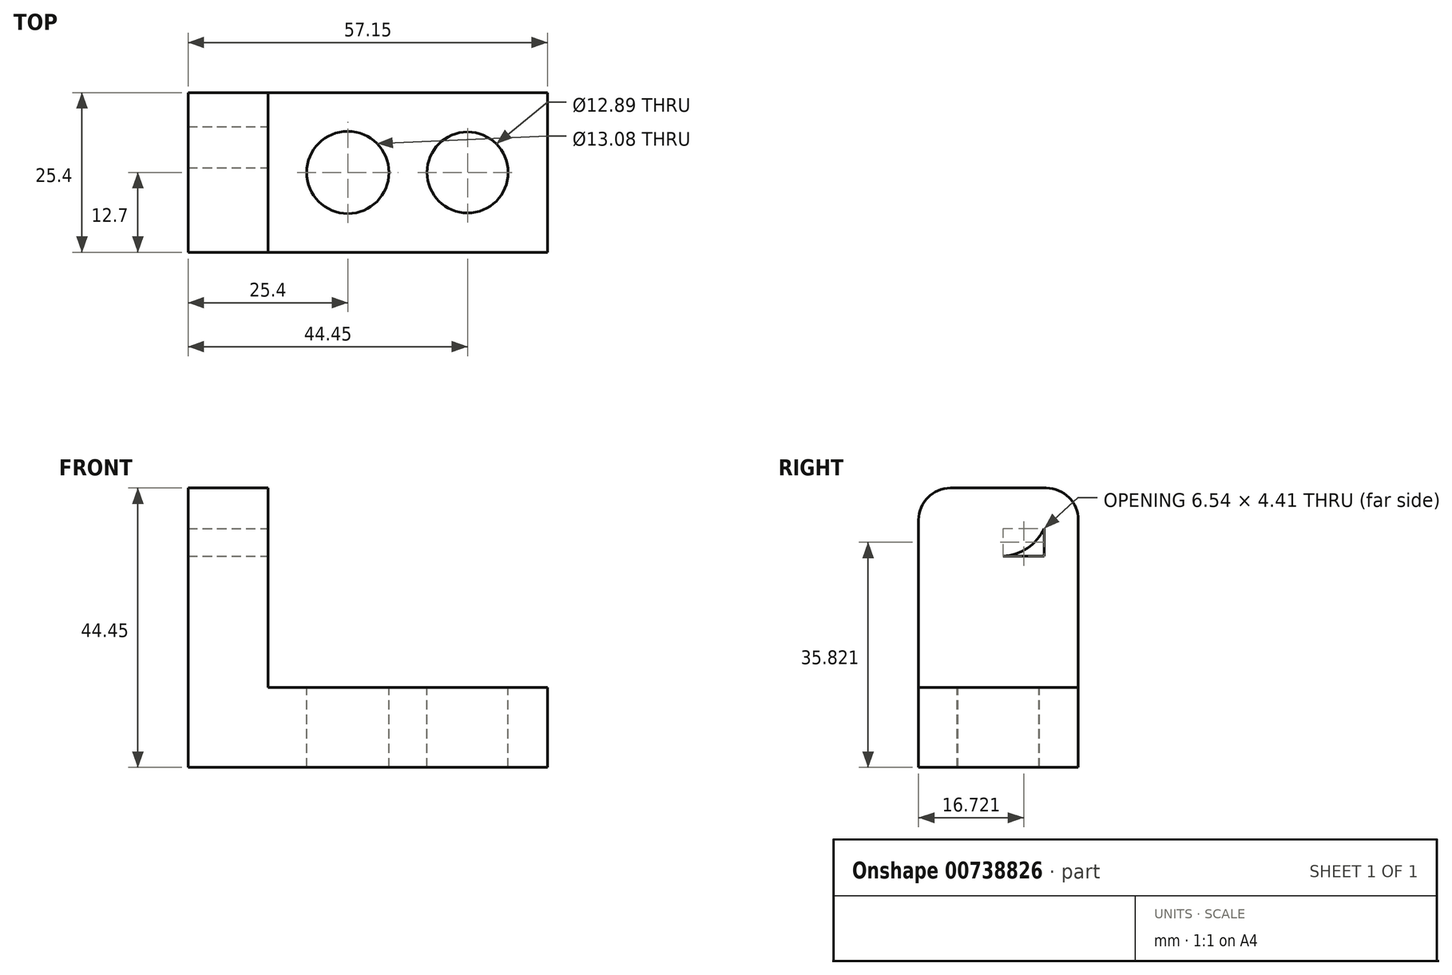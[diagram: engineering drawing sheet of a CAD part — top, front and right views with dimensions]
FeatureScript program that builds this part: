
annotation { "Feature Type Name" : "Feature", "Feature Type Description" : "" }
export const myFeature = defineFeature(function(context is Context, id is Id, definition is map)
    precondition{}
    {
        {
            var Q0;
            Q0=qCreatedBy(makeId("Front.planeOp"),FACE);
            var sketch = newSketch(context, id + "F0", { "sketchPlane" : qUnion([Q0])});
            skLineSegment(sketch, "E0", {"start": v(0, 0) * mm, "end": v(0, 44.45) * mm});
            skLineSegment(sketch, "E1", {"start": v(0, 44.45) * mm, "end": v(57.15, 44.45) * mm});
            skLineSegment(sketch, "E2", {"start": v(57.15, 44.45) * mm, "end": v(57.15, 0) * mm});
            skLineSegment(sketch, "E3", {"start": v(57.15, 0) * mm, "end": v(0, 0) * mm});
            skSolve(sketch);
        }
        {
            var Q0;
            Q0 = qSketchRegion(id + "F0", true);
            extrude(context, id + "F1", {"entities" : qUnion([Q0]), "depth" : 25.4 * mm, "offsetDistance" : 25.4 * mm});
        }
        {
            var Q0;
            Q0=makeQuery(id+"F1.opExtrude","SWEPT_FACE",FACE,{"disambiguationData":[OSD([sQuery(id+"F0.wireOp",EDGE,"E1")])]});
            var sketch = newSketch(context, id + "F2", { "sketchPlane" : qUnion([Q0])});
            skLineSegment(sketch, "E4", {"start": v(12.7, 0) * mm, "end": v(12.7, -25.4) * mm});
            skSolve(sketch);
        }
        {
            var Q0;
            {var subQ0=sQuery(id+"F2.wireOp",EDGE,"E4");Q0=makeQuery(id+"F2.imprint","IMPRINT",FACE,{"disambiguationData":[TD([[makeQuery(id+"F2.imprint","IMPRINT",EDGE,{"derivedFrom":subQ0}),1.0]])]});}
            extrude(context, id + "F3", {"entities" : qUnion([Q0]), "operationType" : NewBodyOperationType.REMOVE, "oppositeDirection" : true, "depth" : 31.75 * mm, "offsetDistance" : 25.4 * mm});
        }
        {
            var Q0;
            Q0=makeQuery(id+"F3.boolean.opBoolean","COPY",FACE,{"derivedFrom":makeQuery(id+"F3.opExtrude","CAP_FACE",FACE,{"disambiguationData":[OSD([sQuery(id+"F0.wireOp",EDGE,"E1"),sQuery(id+"F0.wireOp",EDGE,"E2"),sQuery(id+"F2.wireOp",EDGE,"E4")])],"isStart":false})});
            var sketch = newSketch(context, id + "F4", { "sketchPlane" : qUnion([Q0])});
            skLineSegment(sketch, "E5", {"start": v(12.7, -12.7) * mm, "end": v(57.15, -12.7) * mm});
            skLineSegment(sketch, "E6", {"start": v(25.4, 0) * mm, "end": v(25.4, -25.4) * mm});
            skLineSegment(sketch, "E7", {"start": v(44.45, 0) * mm, "end": v(44.45, -25.4) * mm});
            skCircle(sketch, "E8", {"center": v(25.4, -12.7) * mm, "radius": 6.54 * mm});
            skCircle(sketch, "E9", {"center": v(44.45, -12.7) * mm, "radius": 6.45 * mm});
            skArc(sketch, "E10", {"start": v(44.45, -25.4) * mm, "mid": v(57.19, -12.7) * mm, "end": v(44.45, 0) * mm});
            skSolve(sketch);
        }
        {
            var Q0;
            {var subQ0=sQuery(id+"F4.wireOp",EDGE,"E6");var subQ1=sQuery(id+"F4.wireOp",EDGE,"E5");var subQ2=makeQuery(id+"F4.imprint","INTERSECT",VERTEX,{"derivedFrom":[subQ1,subQ0]});Q0=makeQuery(id+"F4.imprint","IMPRINT",FACE,{"disambiguationData":[TD([[makeQuery(id+"F4.imprint","IMPRINT",EDGE,{"disambiguationData":[TD([[subQ2,-1.0]])],"derivedFrom":subQ1}),1.0]])]});}
            var Q1;
            {var subQ0=sQuery(id+"F4.wireOp",EDGE,"E8");var subQ1=sQuery(id+"F4.wireOp",EDGE,"E5");var subQ2=makeQuery(id+"F4.imprint","INTERSECT",VERTEX,{"disambiguationData":[OD(0.0)],"derivedFrom":[subQ1,subQ0]});Q1=makeQuery(id+"F4.imprint","IMPRINT",FACE,{"disambiguationData":[TD([[makeQuery(id+"F4.imprint","IMPRINT",EDGE,{"disambiguationData":[TD([[subQ2,-1.0]])],"derivedFrom":subQ1}),1.0]])]});}
            var Q2;
            {var subQ0=sQuery(id+"F4.wireOp",EDGE,"E8");var subQ1=sQuery(id+"F4.wireOp",EDGE,"E5");var subQ2=makeQuery(id+"F4.imprint","INTERSECT",VERTEX,{"disambiguationData":[OD(0.0)],"derivedFrom":[subQ1,subQ0]});Q2=makeQuery(id+"F4.imprint","IMPRINT",FACE,{"disambiguationData":[TD([[makeQuery(id+"F4.imprint","IMPRINT",EDGE,{"disambiguationData":[TD([[subQ2,-1.0]])],"derivedFrom":subQ1}),-1.0]])]});}
            var Q3;
            {var subQ0=sQuery(id+"F4.wireOp",EDGE,"E6");var subQ1=sQuery(id+"F4.wireOp",EDGE,"E5");var subQ2=makeQuery(id+"F4.imprint","INTERSECT",VERTEX,{"derivedFrom":[subQ1,subQ0]});Q3=makeQuery(id+"F4.imprint","IMPRINT",FACE,{"disambiguationData":[TD([[makeQuery(id+"F4.imprint","IMPRINT",EDGE,{"disambiguationData":[TD([[subQ2,-1.0]])],"derivedFrom":subQ1}),-1.0]])]});}
            var Q4;
            {var subQ0=sQuery(id+"F4.wireOp",EDGE,"E9");var subQ1=sQuery(id+"F4.wireOp",EDGE,"E5");var subQ2=makeQuery(id+"F4.imprint","INTERSECT",VERTEX,{"disambiguationData":[OD(0.0)],"derivedFrom":[subQ1,subQ0]});Q4=makeQuery(id+"F4.imprint","IMPRINT",FACE,{"disambiguationData":[TD([[makeQuery(id+"F4.imprint","IMPRINT",EDGE,{"disambiguationData":[TD([[subQ2,-1.0]])],"derivedFrom":subQ1}),1.0]])]});}
            var Q5;
            {var subQ0=sQuery(id+"F4.wireOp",EDGE,"E7");var subQ1=sQuery(id+"F4.wireOp",EDGE,"E5");var subQ2=makeQuery(id+"F4.imprint","INTERSECT",VERTEX,{"derivedFrom":[subQ1,subQ0]});Q5=makeQuery(id+"F4.imprint","IMPRINT",FACE,{"disambiguationData":[TD([[makeQuery(id+"F4.imprint","IMPRINT",EDGE,{"disambiguationData":[TD([[subQ2,-1.0]])],"derivedFrom":subQ1}),1.0]])]});}
            var Q6;
            {var subQ0=sQuery(id+"F4.wireOp",EDGE,"E9");var subQ1=sQuery(id+"F4.wireOp",EDGE,"E5");var subQ2=makeQuery(id+"F4.imprint","INTERSECT",VERTEX,{"disambiguationData":[OD(0.0)],"derivedFrom":[subQ1,subQ0]});Q6=makeQuery(id+"F4.imprint","IMPRINT",FACE,{"disambiguationData":[TD([[makeQuery(id+"F4.imprint","IMPRINT",EDGE,{"disambiguationData":[TD([[subQ2,-1.0]])],"derivedFrom":subQ1}),-1.0]])]});}
            var Q7;
            {var subQ0=sQuery(id+"F4.wireOp",EDGE,"E7");var subQ1=sQuery(id+"F4.wireOp",EDGE,"E5");var subQ2=makeQuery(id+"F4.imprint","INTERSECT",VERTEX,{"derivedFrom":[subQ1,subQ0]});Q7=makeQuery(id+"F4.imprint","IMPRINT",FACE,{"disambiguationData":[TD([[makeQuery(id+"F4.imprint","IMPRINT",EDGE,{"disambiguationData":[TD([[subQ2,-1.0]])],"derivedFrom":subQ1}),-1.0]])]});}
            var Q8;
            {var subQ0=sQuery(id+"F4.wireOp",EDGE,"E10");var subQ1=sQuery(id+"F0.wireOp",EDGE,"E1");var subQ3=sQuery(id+"F0.wireOp",EDGE,"E2");var subQ6=makeQuery(id+"F3.boolean.opBoolean","COPY",EDGE,{"derivedFrom":makeQuery(id+"F3.opExtrude","CAP_EDGE",EDGE,{"disambiguationData":[OSD([subQ1,subQ3])],"isStart":false})});var subQ7=makeQuery(id+"F4.imprint","INTERSECT",VERTEX,{"disambiguationData":[OD(1.0)],"derivedFrom":[subQ6,subQ0]});Q8=makeQuery(id+"F4.imprint","IMPRINT",FACE,{"disambiguationData":[TD([[makeQuery(id+"F4.imprint","IMPRINT",EDGE,{"disambiguationData":[TD([[subQ7,-1.0]])],"derivedFrom":subQ0}),-1.0]])]});}
            var Q9;
            {var subQ0=sQuery(id+"F4.wireOp",EDGE,"E10");var subQ1=sQuery(id+"F0.wireOp",EDGE,"E1");var subQ3=sQuery(id+"F0.wireOp",EDGE,"E2");var subQ6=makeQuery(id+"F3.boolean.opBoolean","COPY",EDGE,{"derivedFrom":makeQuery(id+"F3.opExtrude","CAP_EDGE",EDGE,{"disambiguationData":[OSD([subQ1,subQ3])],"isStart":false})});var subQ7=makeQuery(id+"F4.imprint","INTERSECT",VERTEX,{"disambiguationData":[OD(0.0)],"derivedFrom":[subQ6,subQ0]});Q9=makeQuery(id+"F4.imprint","IMPRINT",FACE,{"disambiguationData":[TD([[makeQuery(id+"F4.imprint","IMPRINT",EDGE,{"disambiguationData":[TD([[subQ7,1.0]])],"derivedFrom":subQ0}),-1.0]])]});}
            extrude(context, id + "F5", {"entities" : qUnion([Q0, Q1, Q2, Q3, Q4, Q5, Q6, Q7, Q8, Q9]), "operationType" : NewBodyOperationType.REMOVE, "endBound" : BoundingType.THROUGH_ALL, "oppositeDirection" : true, "depth" : 25.4 * mm, "offsetDistance" : 25.4 * mm});
        }
        {
            var Q0;
            Q0=makeQuery(id+"F3.boolean.opBoolean","COPY",FACE,{"derivedFrom":makeQuery(id+"F3.opExtrude","SWEPT_FACE",FACE,{"disambiguationData":[OSD([sQuery(id+"F2.wireOp",EDGE,"E4")])]})});
            var sketch = newSketch(context, id + "F6", { "sketchPlane" : qUnion([Q0])});
            skLineSegment(sketch, "E11", {"start": v(-19.25, 44.45) * mm, "end": v(-19.25, 12.7) * mm});
            skLineSegment(sketch, "E12", {"start": v(-5.41, 44.45) * mm, "end": v(-5.41, 12.7) * mm});
            skLineSegment(sketch, "E13", {"start": v(-25.4, 33.62) * mm, "end": v(0, 33.62) * mm});
            skArc(sketch, "E14", {"start": v(-19.25, 44.45) * mm, "mid": v(-12.33, 33.6) * mm, "end": v(-5.41, 44.45) * mm});
            skSolve(sketch);
        }
        {
            var Q0;
            {var subQ0=sQuery(id+"F6.wireOp",EDGE,"E14");var subQ3=sQuery(id+"F6.wireOp",EDGE,"E13");var subQ4=makeQuery(id+"F6.imprint","INTERSECT",VERTEX,{"disambiguationData":[OD(0.0)],"derivedFrom":[subQ3,subQ0]});Q0=makeQuery(id+"F6.imprint","IMPRINT",FACE,{"disambiguationData":[TD([[makeQuery(id+"F6.imprint","IMPRINT",EDGE,{"disambiguationData":[TD([[subQ4,-1.0]])],"derivedFrom":subQ3}),1.0]])]});}
            extrude(context, id + "F7", {"entities" : qUnion([Q0]), "operationType" : NewBodyOperationType.REMOVE, "endBound" : BoundingType.THROUGH_ALL, "oppositeDirection" : true, "depth" : 25.4 * mm, "offsetDistance" : 25.4 * mm});
        }
        {
            var Q0;
            Q0=makeQuery(id+"F1.opExtrude","CAP_EDGE",EDGE,{"disambiguationData":[OSD([sQuery(id+"F0.wireOp",EDGE,"E1")])],"isStart":true});
            var Q1;
            Q1=makeQuery(id+"F1.opExtrude","CAP_EDGE",EDGE,{"disambiguationData":[OSD([sQuery(id+"F0.wireOp",EDGE,"E1")])],"isStart":false});
            fillet(context, id + "F8", {"entities" : qUnion([Q0, Q1]), "radius" : 5.08 * mm, "tangentPropagation" : true, "allowEdgeOverflow" : false});
        }
    });
